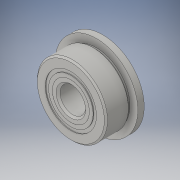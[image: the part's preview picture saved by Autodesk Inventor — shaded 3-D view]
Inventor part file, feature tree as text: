
AUTODESK INVENTOR PART (.ipt)
format: ipt  version: 2016 (Build 200138000, 138)  size: 589,824 bytes
history: native  units: in
note: dims shown in document units (in); Inventor stores cm internally (conversion verified against a paired STEP export)
features: other x10, revolve x5
ambient origin geometry x8: Origin, YZ Plane, XZ Plane, XY Plane, X Axis, Y Axis, Z Axis, Center Point
bodies: Solid1 (feature_tree), Solid2 (feature_tree), Solid3 (feature_tree), Solid4 (feature_tree), Solid5 (feature_tree), Solid6 (feature_tree), Solid7 (feature_tree), Solid8 (feature_tree), Solid9 (feature_tree), Solid10 (feature_tree), Solid11 (feature_tree), Solid12 (feature_tree), Solid13 (feature_tree), Solid14 (feature_tree), Solid15 (feature_tree)
feature tree (15):
  revolve  "Revolve2"  [1 undecoded]
  revolve  "Revolve3"  [1 undecoded]
  other  "Cut-Revolve1"
  revolve  "Revolve4"  [1 undecoded]
  other  "CirPattern1[1]"
  other  "CirPattern1[2]"
  other  "CirPattern1[3]"
  other  "CirPattern1[4]"
  other  "CirPattern1[5]"
  other  "CirPattern1[6]"
  other  "CirPattern1[7]"
  other  "CirPattern1[8]"
  other  "CirPattern1[9]"
  revolve  "Revolve6[1]"  [1 undecoded]
  revolve  "Revolve6[2]"  [1 undecoded]
note: 5 required parameter values undecoded (feature->parameter linkage not recoverable at this tier; creation-order binding heuristic only, values carry confidence <= 0.55)
